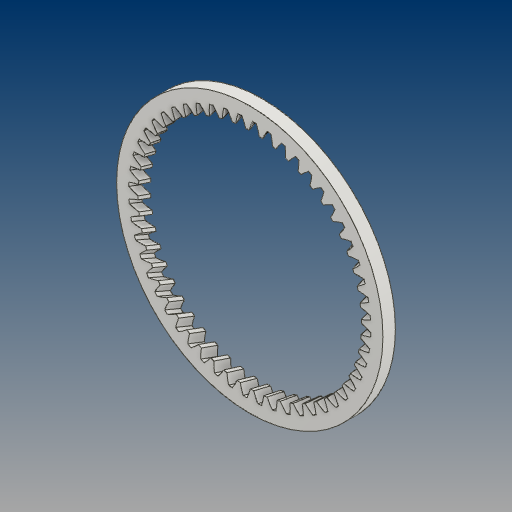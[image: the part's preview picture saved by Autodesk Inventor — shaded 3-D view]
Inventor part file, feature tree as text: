
AUTODESK INVENTOR PART (.ipt)
format: ipt  version: 2021 (Build 250183000, 183)  size: 739,840 bytes
history: native  units: mm (DEFAULTED — no unit token found)
features: plane x3, other x3, sketch x2, extrude x1
ambient origin geometry x8: Origin, YZ Plane, XZ Plane, XY Plane, X Axis, Y Axis, Z Axis, Center Point
bodies: Solid1 (feature_tree)
feature tree (9):
  extrude  "Extrusion1"  Depth=15.0mm TaperAngle=0.0deg
  plane  "Work Plane2"
  plane  "Work Plane8"
  plane  "Work Plane9"
  other  "Spur Gear"
  sketch  "Sketch1"  dims[d0=319.990604mm d1=15.0mm d2=0.0mm]
  sketch  "Sketch2"  dims[d3=276.686221mm d4=10.0mm d5=0.0mm d16=70.0mm d17=0.0mm d34=0.604152mm d39=0.0mm d45=0.0mm d47=70.0mm d50=0.0mm d51=0.0mm d52=70.0mm]
  other  "Srf1"
  other  "Pitch Diameter"
